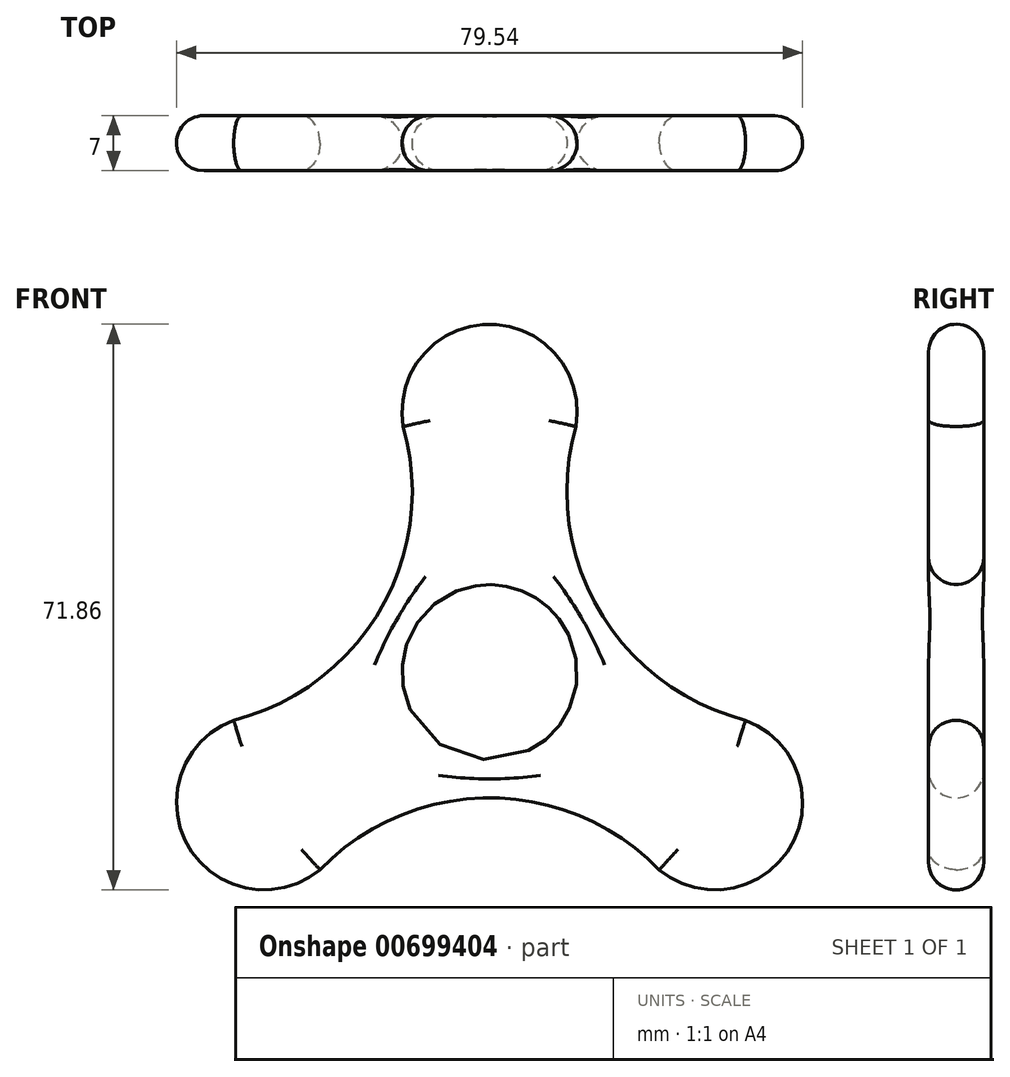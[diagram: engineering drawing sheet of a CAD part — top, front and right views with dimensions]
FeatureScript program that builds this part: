
annotation { "Feature Type Name" : "Feature", "Feature Type Description" : "" }
export const myFeature = defineFeature(function(context is Context, id is Id, definition is map)
    precondition{}
    {
        {
            var Q0;
            Q0=qCreatedBy(makeId("Front.planeOp"),FACE);
            var sketch = newSketch(context, id + "F0", { "sketchPlane" : qUnion([Q0])});
            skCircle(sketch, "E0", {"center": v(0, 0) * mm, "radius": 11.12 * mm});
            skCircle(sketch, "E1", {"center": v(0, 33.08) * mm, "radius": 11.12 * mm});
            skCircle(sketch, "E2.1.1", {"center": v(-28.65, -16.54) * mm, "radius": 11.12 * mm});
            skCircle(sketch, "E2.2.1", {"center": v(28.65, -16.54) * mm, "radius": 11.12 * mm});
            skArc(sketch, "E3", {"start": v(-32.51, -6.1) * mm, "mid": v(-13.84, 7.99) * mm, "end": v(-10.97, 31.2) * mm});
            skArc(sketch, "E4", {"start": v(21.54, -25.1) * mm, "mid": v(0, -15.98) * mm, "end": v(-21.54, -25.1) * mm});
            skArc(sketch, "E5", {"start": v(10.97, 31.2) * mm, "mid": v(13.84, 7.99) * mm, "end": v(32.51, -6.1) * mm});
            skSolve(sketch);
        }
        {
            var Q0;
            Q0=makeQuery(id+"F0.imprint","IMPRINT",FACE,{"disambiguationData":[TD([[makeQuery(id+"F0.imprint","IMPRINT",EDGE,{"derivedFrom":sQuery(id+"F0.wireOp",EDGE,"E0")}),-1.0]])]});
            var Q1;
            {var subQ0=sQuery(id+"F0.wireOp",EDGE,"E4");var subQ1=sQuery(id+"F0.wireOp",EDGE,"E2.1.1");var subQ2=makeQuery(id+"F0.imprint","INTERSECT",VERTEX,{"disambiguationData":[OD(1.0)],"derivedFrom":[subQ1,subQ0]});Q1=makeQuery(id+"F0.imprint","IMPRINT",FACE,{"disambiguationData":[TD([[makeQuery(id+"F0.imprint","IMPRINT",EDGE,{"disambiguationData":[TD([[subQ2,-1.0]])],"derivedFrom":subQ1}),1.0]])]});}
            var Q2;
            {var subQ0=sQuery(id+"F0.wireOp",EDGE,"E3");var subQ1=sQuery(id+"F0.wireOp",EDGE,"E1");var subQ2=makeQuery(id+"F0.imprint","INTERSECT",VERTEX,{"disambiguationData":[OD(1.0)],"derivedFrom":[subQ1,subQ0]});Q2=makeQuery(id+"F0.imprint","IMPRINT",FACE,{"disambiguationData":[TD([[makeQuery(id+"F0.imprint","IMPRINT",EDGE,{"disambiguationData":[TD([[subQ2,-1.0]])],"derivedFrom":subQ1}),1.0]])]});}
            var Q3;
            {var subQ0=sQuery(id+"F0.wireOp",EDGE,"E5");var subQ1=sQuery(id+"F0.wireOp",EDGE,"E2.2.1");var subQ2=makeQuery(id+"F0.imprint","INTERSECT",VERTEX,{"disambiguationData":[OD(1.0)],"derivedFrom":[subQ1,subQ0]});Q3=makeQuery(id+"F0.imprint","IMPRINT",FACE,{"disambiguationData":[TD([[makeQuery(id+"F0.imprint","IMPRINT",EDGE,{"disambiguationData":[TD([[subQ2,-1.0]])],"derivedFrom":subQ1}),1.0]])]});}
            extrude(context, id + "F1", {"entities" : qUnion([Q0, Q1, Q2, Q3]), "depth" : 7 * mm, "offsetDistance" : 25 * mm});
        }
        {
            var Q0;
            Q0=makeQuery(id+"F1.opExtrude","CAP_FACE",FACE,{"disambiguationData":[OSD([sQuery(id+"F0.wireOp",EDGE,"E1"),sQuery(id+"F0.wireOp",EDGE,"E2.1.1"),sQuery(id+"F0.wireOp",EDGE,"E0"),sQuery(id+"F0.wireOp",EDGE,"E2.2.1"),sQuery(id+"F0.wireOp",EDGE,"E3"),sQuery(id+"F0.wireOp",EDGE,"E4"),sQuery(id+"F0.wireOp",EDGE,"E5")])],"isStart":false});
            fillet(context, id + "F2", {"entities" : qUnion([Q0]), "radius" : 3.5 * mm, "tangentPropagation" : true, "allowEdgeOverflow" : false});
        }
        {
            var Q0;
            Q0=makeQuery(id+"F1.opExtrude","CAP_FACE",FACE,{"disambiguationData":[OSD([sQuery(id+"F0.wireOp",EDGE,"E1"),sQuery(id+"F0.wireOp",EDGE,"E2.1.1"),sQuery(id+"F0.wireOp",EDGE,"E0"),sQuery(id+"F0.wireOp",EDGE,"E2.2.1"),sQuery(id+"F0.wireOp",EDGE,"E3"),sQuery(id+"F0.wireOp",EDGE,"E4"),sQuery(id+"F0.wireOp",EDGE,"E5")])],"isStart":true});
            fillet(context, id + "F3", {"entities" : qUnion([Q0]), "radius" : 3.5 * mm, "tangentPropagation" : true, "allowEdgeOverflow" : false});
        }
    });
